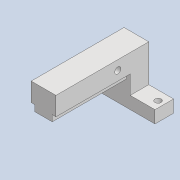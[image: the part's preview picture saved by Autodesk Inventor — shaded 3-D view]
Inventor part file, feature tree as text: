
AUTODESK INVENTOR PART (.ipt)
format: ipt  version: 2020 (Build 240168000, 168)  size: 144,384 bytes
history: native  units: mm
features: sketch x4, extrude x2, hole x2
ambient origin geometry x8: Origin, YZ Plane, XZ Plane, XY Plane, X Axis, Y Axis, Z Axis, Center Point
bodies: Solid1 (feature_tree)
feature tree (8):
  extrude  "Extrusion1"  Depth=60.0mm
  hole  "Hole1"  [1 undecoded]
  extrude  "Extrusion2"  Depth=50.0mm
  hole  "Hole2"  [1 undecoded]
  sketch  "Sketch1"  dims[d0=10.0mm d1=60.0mm]
  sketch  "Sketch2"  dims[d2=30.0mm d3=20.0mm]
  sketch  "Sketch3"  dims[d4=15.0mm d5=0.0mm d6=50.0mm]
  sketch  "Sketch4"  dims[d7=5.0mm d8=6.0mm d9=4.0mm d10=2.0mm d11=90.0deg d12=8.0mm d13=20.594885mm d14=20.0mm d15=3.0mm d16=5.0mm d17=35.0mm d18=0.0mm d20=5.0mm d21=6.0mm d22=9.0mm d23=5.0mm d24=90.0deg d25=8.0mm d26=20.594885mm d27=25.0mm]
note: 2 required parameter values undecoded (feature->parameter linkage not recoverable at this tier; creation-order binding heuristic only, values carry confidence <= 0.55)
